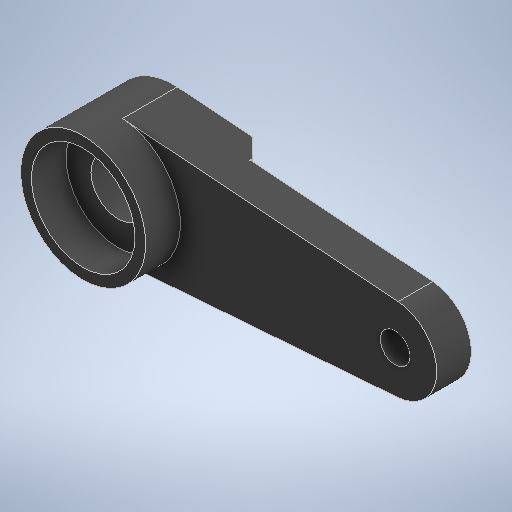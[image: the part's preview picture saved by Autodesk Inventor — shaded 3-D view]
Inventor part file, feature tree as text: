
AUTODESK INVENTOR PART (.ipt)
format: ipt  version: 2025.1 (Build 291241000, 241)  size: 287,232 bytes
history: native  units: in
note: dims shown in document units (in); Inventor stores cm internally (conversion verified against a paired STEP export)
features: extrude x3, sketch x1, chamfer x1
ambient origin geometry x8: Origin, YZ Plane, XZ Plane, XY Plane, X Axis, Y Axis, Z Axis, Center Point
bodies: Solid1 (feature_tree)
feature tree (5):
  sketch  "Sketch1"  dims[d0=0.2835in d1=0.189in d2=0.628in d3=0.0787in d4=0.0in d5=0.3622in d6=0.122in d7=0.0669in d8=0.0453in d9=0.0in d10=0.2343in d11=0.1575in d12=0.0in d13=0.0394in d14=0.0787in d15=45.0deg]
  extrude  "Extrusion1"  Depth=0.0787in
  extrude  "Extrusion2"  Depth=0.628in
  extrude  "Extrusion3"  Depth=0.0787in TaperAngle=0.0deg
  chamfer  "Chamfer1"  Distance=0.3622in
